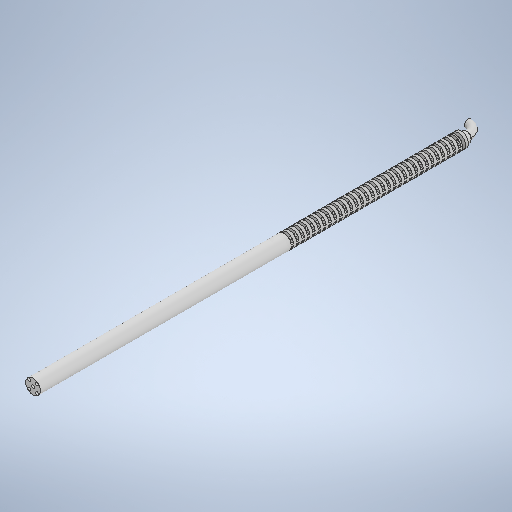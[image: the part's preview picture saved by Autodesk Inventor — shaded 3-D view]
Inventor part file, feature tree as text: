
AUTODESK INVENTOR PART (.ipt)
format: ipt  version: 2025.2 (Build 292293000, 293)  size: 800,256 bytes
history: native  units: mm
features: sketch x18, extrude x12, plane x3, sweep x1
ambient origin geometry x8: Origin, YZ Plane, XZ Plane, XY Plane, X Axis, Y Axis, Z Axis, Center Point
bodies: Solid1 (feature_tree)
feature tree (34):
  extrude  "Extrusion1"  Depth=40.0mm TaperAngle=0.0deg
  plane  "Work Plane1"
  extrude  "Extrusion2"  Depth=1.3mm
  extrude  "Extrusion3"  Depth=0.5mm
  extrude  "Extrusion4"  Depth=40.0mm
  sketch  "Sketch5"  dims[d11=0.3mm d12=0.3mm]
  extrude  "Extrusion5"  Depth=0.3mm
  extrude  "Extrusion6"  Depth=0.3mm
  extrude  "Extrusion7"  Depth=0.6mm
  plane  "Work Plane2"
  extrude  "Extrusion9"  Depth=0.6mm
  extrude  "Extrusion10"  Depth=40.0mm TaperAngle=360.0deg
  extrude  "Extrusion11"  Depth=0.6mm TaperAngle=0.0deg
  extrude  "Extrusion12"  Depth=0.6mm TaperAngle=0.0deg
  sketch  "Sketch17"  dims[d43=0.2mm]
  sketch  "Sketch18"  dims[d44=0.5mm]
  extrude  "Extrusion13"  Depth=4.0mm
  plane  "Work Plane3"
  sweep  "Sweep1"
  sketch  "Sketch1"  dims[d0=3.0mm d1=40.0mm d2=0.0mm]
  sketch  "Sketch2"  dims[d5=0.5mm d6=0.5mm]
  sketch  "Sketch3"  dims[d7=0.6mm d8=40.0mm]
  sketch  "Sketch4"  dims[d9=0.3mm d10=0.3mm]
  sketch  "Sketch Circular Pattern1"  dims[d3=-40.0mm d4=1.3mm]
  sketch  "Sketch6"  dims[d13=54.75mm d14=5.0mm d15=0.0mm d16=0.0mm d17=0.6mm]
  sketch  "Sketch7"  dims[d20=54.75mm d21=0.0mm d22=0.6mm]
  sketch  "Sketch8"  dims[d23=2.3mm d24=40.0mm d26=360.0deg]
  sketch  "Sketch10"  dims[d28=54.75mm d29=0.0mm d30=0.6mm d31=0.0mm]
  sketch  "Sketch11"  dims[d32=0.6mm d33=0.0mm d34=0.6mm d35=0.0mm]
  sketch  "Sketch14"  dims[d38=-13.25mm d39=4.0mm]
  sketch  "Sketch15"  dims[d40=0.1mm d41=20.75mm d42=0.0mm]
  sketch  "Sketch19"  dims[d45=2.0mm]
  sketch  "Sketch20"  dims[d48=0.25mm]
  sketch  "Sketch21"  dims[d51=0.75mm d52=0.2mm d53=0.2mm d54=2.591063mm d55=0.5mm d56=0.1mm d57=0.2mm d58=0.25mm d59=2.5mm d60=2.5mm d61=20.754mm d62=0.0mm d63=46.004mm d64=0.0mm d65=46.004mm d66=0.0mm d67=1.0mm d68=1.0mm d69=1.0mm d70=0.0mm d71=0.0mm d72=0.3mm d73=0.0mm d74=0.0mm d76=0.5mm d77=0.872665mm d78=0.5mm d79=0.872665mm]
